# Revit family: Wall_Expansion_Joint-Emseal-Emshield-WFR1-(0.5-6-Inch)
name_source: partatom
category: Specialty Equipment
units: mm (PartAtom-declared; Revit-internal decimal feet)

## family parameters
Cut with Voids When Loaded = No
Host = Face
OmniClass Number = 23.25.30.24
OmniClass Title = Structural Walls
Part Type = Normal
Room Calculation Point = No
Round Connector Dimension = Use Diameter
Shared = No

## types (1)
- REFER TO TYPE CATALOG
    ABAA Compliance = YES
    Air Permeability (ASTM E283-04) = 0.00017 L/(s-m²) @ 75 Delta-P(Pa) 0.00017 L(s-m²) @ 250 Delta-P(Pa)
    Assembly Code = B2010
    Default Elevation = 4' - 0"
    Depth = 0' - 4"
    Description = Fire Rated, Watertight, Sound Dampening, Primary Seal for Interior and Exterior Wall Expansion Joints
    Durometer Hardness of Silicone Coating (ASTM D2240) = Shore A: 15
    Fire Rated Movement Rating (UL2079) = Class II, III
    Fire Rating (Hours per UL2079) = 1
    Fire Resistance and Movement Cycling Regime (UL 2079, ASTM E1966, ASTM E119, ASTM E1399) = Passed
    Host Thickness = -0' - 4"
    Manufacturer = Emseal Joint Systems, Ltd.
    Model = WFR1
    Movement (of Nominal Material Size) = + 50% / - 50%
    OITC Rating (Outdoor/Indoor Transmission Class) = OITC 52 (in a OITC 52 wall)
    Pick Resistant = No
    Product Documentation Link = https://cdn.emseal.com
    Product Page URL = https://www.emseal.com
    Product data url = https://cdn.emseal.com
    R Value Range (ASTM C518) = 1.03 per 1-inch (25mm) depth
    Rate of Air Leakage (ASTM E283) = Passed
    STC Rating (Sound Transmission Class) (ASTM E90) = STC 62 (in a STC 68 wall)
    Seal Material = Silicone - Sikasil WS-295
    Seal Material Note = WFR1 has layers of silicone on both sides
    Staining (ASTM C510) = None
    Standard Test Method For Structural Performance of Exterior Windows, Doors, Sylights and Curtain Walls by Uniform Static Air Pressure Difference (ASTM E330) = 1.9mm @ 4854Pa (200mph) 6-Inch width
    Temperature Range (ASTM C711) = 185°F (85°C) to -40°F (-40°C)
    Tensile Strength (ASTM D3574) = 21 psi min;  145 kPa
    Thermal Conductivity (ASTM C518) = 0.9824 BTU*in/h*ft^2*F (0.1417 W/m*K)
    Tornado Resistance (Air Leakage) (ASTM E283) = Tested to 200 mph with essentially no deflection
    Type Image = <None>
    URL = https://www.emseal.com
    Water Penetration of Curtain Wall By Uniform Static Air Pressure Difference (ASTM E331-00) = No water penetration - 15 minute duration at 500 Delta-P(Pa), 1000 Delta-P(Pa),  and 5000 Delta-P(Pa)
    Width = 0' - 0 1/2"

## geometry (parser evidence)
native form markers: Sweep x5
no freeform markers — native parametric forms only
